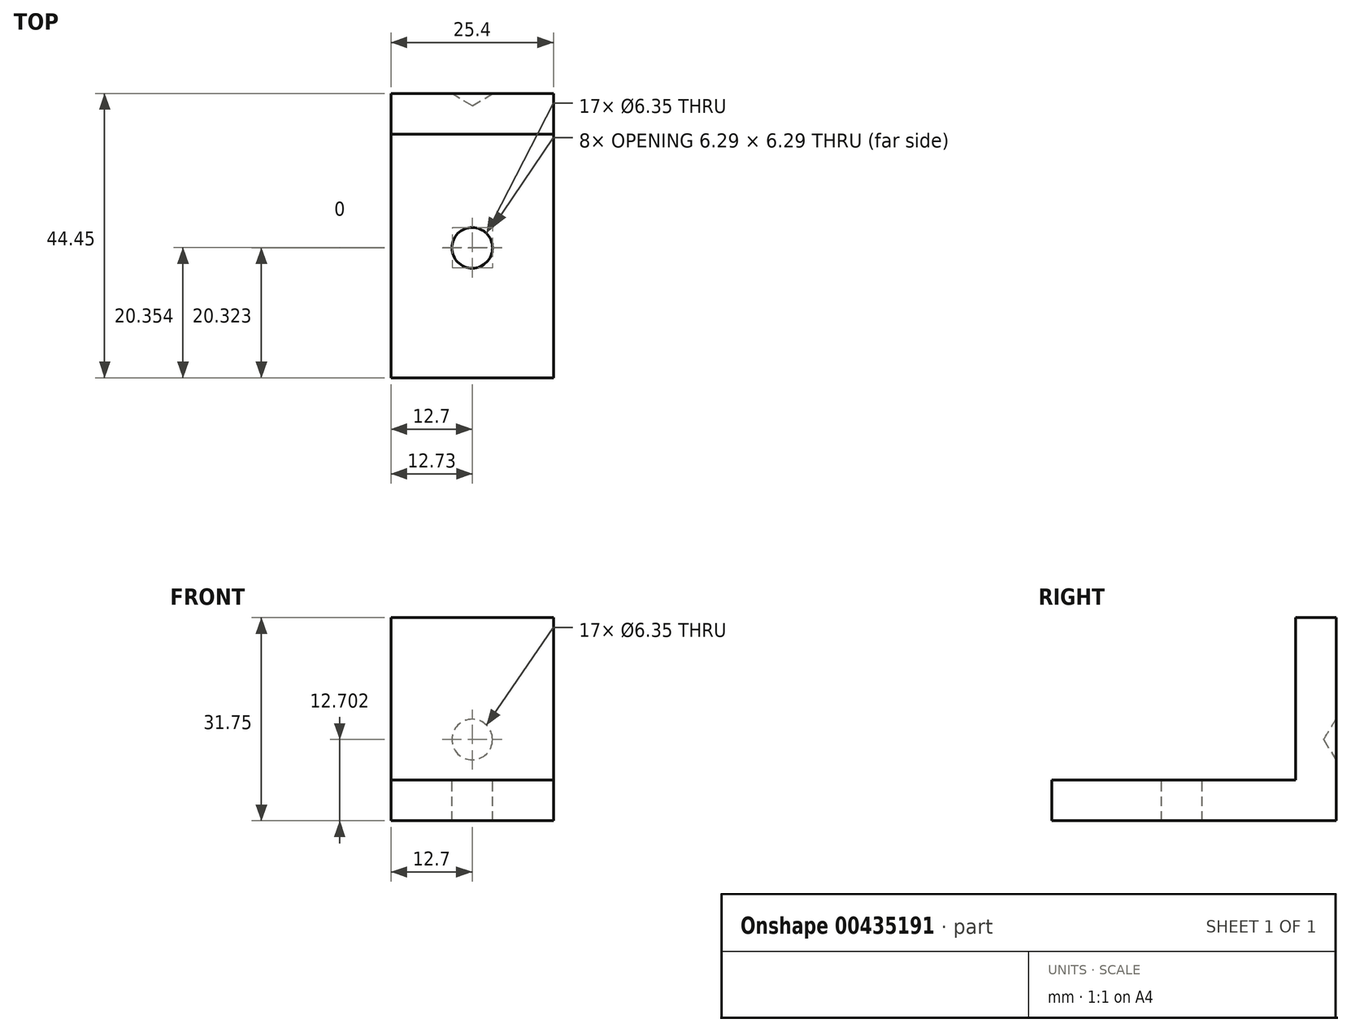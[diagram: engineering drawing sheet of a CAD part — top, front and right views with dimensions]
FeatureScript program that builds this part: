
annotation { "Feature Type Name" : "Feature", "Feature Type Description" : "" }
export const myFeature = defineFeature(function(context is Context, id is Id, definition is map)
    precondition{}
    {
        {
            var Q0;
            Q0=qCreatedBy(makeId("Right.planeOp"),FACE);
            var sketch = newSketch(context, id + "F0", { "sketchPlane" : qUnion([Q0])});
            skLineSegment(sketch, "E0", {"start": v(12.65, 19.15) * mm, "end": v(12.65, -6.25) * mm});
            skLineSegment(sketch, "E1", {"start": v(12.65, -6.25) * mm, "end": v(-25.45, -6.25) * mm});
            skLineSegment(sketch, "E2.0", {"start": v(19, -12.6) * mm, "end": v(-25.45, -12.6) * mm});
            skLineSegment(sketch, "E2.1", {"start": v(19, 19.15) * mm, "end": v(19, -12.6) * mm});
            skLineSegment(sketch, "E3", {"start": v(12.65, 19.15) * mm, "end": v(19, 19.15) * mm});
            skLineSegment(sketch, "E4", {"start": v(-25.45, -6.25) * mm, "end": v(-25.45, -12.6) * mm});
            skSolve(sketch);
        }
        {
            var Q0;
            Q0 = qSketchRegion(id + "F0", true);
            extrude(context, id + "F1", {"entities" : qUnion([Q0]), "depth" : 25.4 * mm});
        }
        {
            var Q0;
            Q0=makeQuery(id+"F1.opExtrude","SWEPT_FACE",FACE,{"disambiguationData":[OSD([sQuery(id+"F0.wireOp",EDGE,"E2.1")])]});
            var sketch = newSketch(context, id + "F2", { "sketchPlane" : qUnion([Q0])});
            skLineSegment(sketch, "E5", {"start": v(-12.7, -12.6) * mm, "end": v(-12.7, 0.1) * mm});
            skSolve(sketch);
        }
        {
            var Q0;
            Q0=sQuery(id+"F2.wireOp",VERTEX,"E5.end");
            var Q1;
            Q1=makeQuery(id+"F1.opExtrude","SWEPT_BODY",BODY,{"disambiguationData":[OSD([sQuery(id+"F0.wireOp",EDGE,"E0"),sQuery(id+"F0.wireOp",EDGE,"E1"),sQuery(id+"F0.wireOp",EDGE,"E2.0"),sQuery(id+"F0.wireOp",EDGE,"E2.1"),sQuery(id+"F0.wireOp",EDGE,"E3"),sQuery(id+"F0.wireOp",EDGE,"E4")])]});
            hole(context, id + "F3", {"style" : HoleStyle.SIMPLE, "endStyle" : HoleEndStyle.BLIND, "holeDiameter" : 6.35 * mm, "holeDepth" : 0.03 * mm, "isTappedThrough" : true, "tappedDepth" : 12.7 * mm, "tapClearance" : 3, "locations" : qUnion([Q0]), "scope" : qUnion([Q1])});
        }
        {
            var Q0;
            Q0=makeQuery(id+"F1.opExtrude","SWEPT_FACE",FACE,{"disambiguationData":[OSD([sQuery(id+"F0.wireOp",EDGE,"E1")])]});
            var sketch = newSketch(context, id + "F4", { "sketchPlane" : qUnion([Q0])});
            skLineSegment(sketch, "E6", {"start": v(12.7, -25.45) * mm, "end": v(12.7, -5.13) * mm});
            skSolve(sketch);
        }
        {
            var Q0;
            Q0=sQuery(id+"F4.wireOp",VERTEX,"E6.end");
            var Q1;
            Q1=makeQuery(id+"F1.opExtrude","SWEPT_BODY",BODY,{"disambiguationData":[OSD([sQuery(id+"F0.wireOp",EDGE,"E0"),sQuery(id+"F0.wireOp",EDGE,"E1"),sQuery(id+"F0.wireOp",EDGE,"E2.0"),sQuery(id+"F0.wireOp",EDGE,"E2.1"),sQuery(id+"F0.wireOp",EDGE,"E3"),sQuery(id+"F0.wireOp",EDGE,"E4")])]});
            hole(context, id + "F5", {"style" : HoleStyle.SIMPLE, "endStyle" : HoleEndStyle.THROUGH, "holeDiameter" : 6.35 * mm, "isTappedThrough" : true, "tappedDepth" : 12.7 * mm, "tapClearance" : 3, "locations" : qUnion([Q0]), "scope" : qUnion([Q1])});
        }
    });
